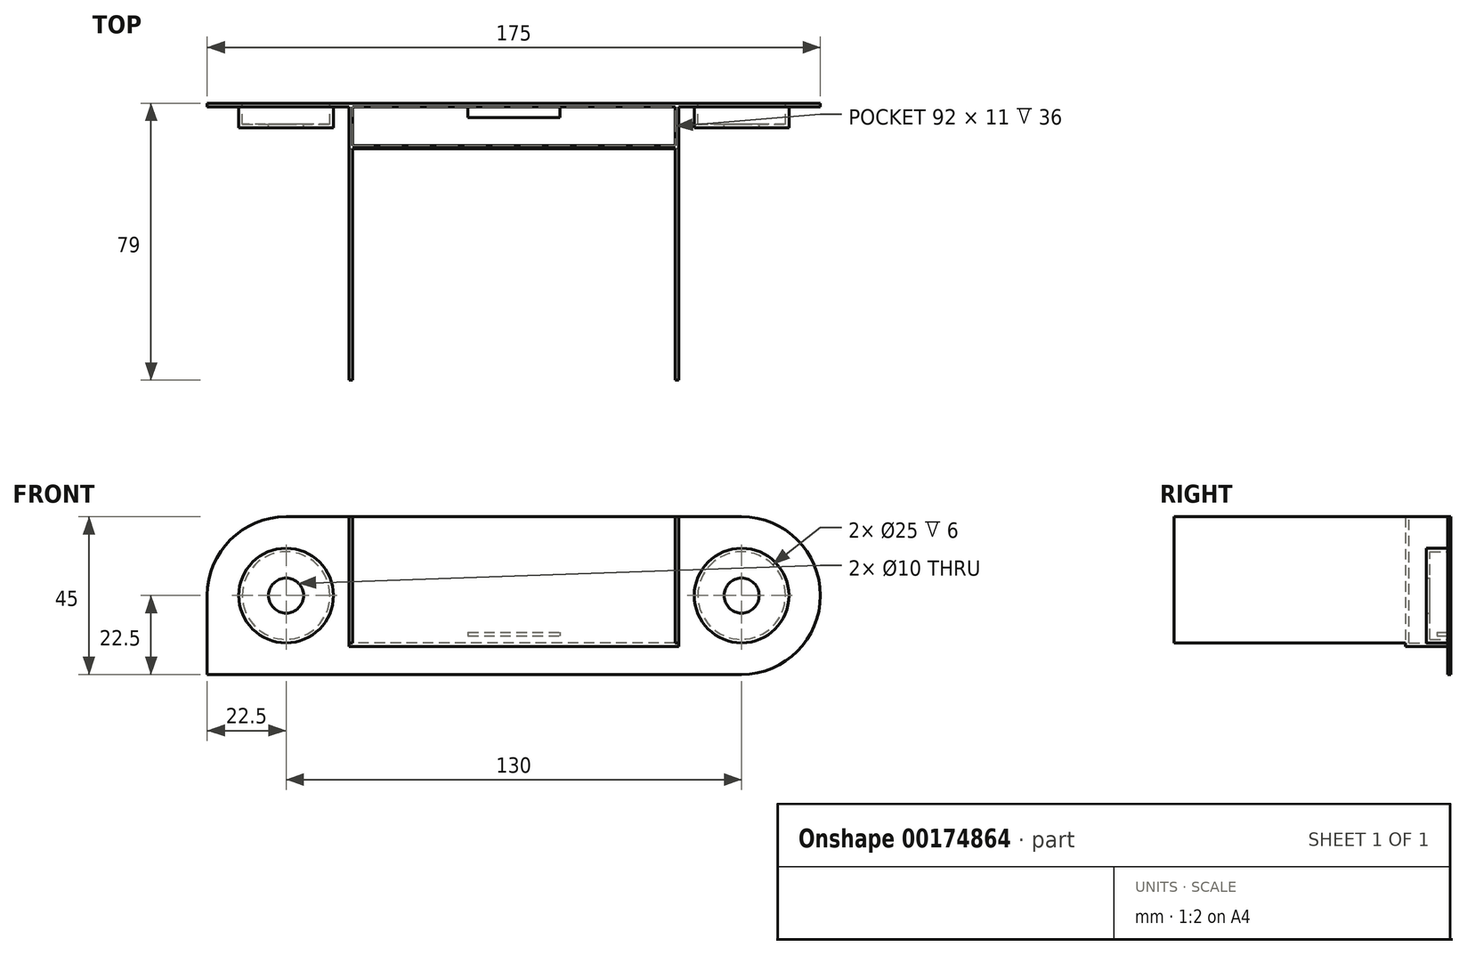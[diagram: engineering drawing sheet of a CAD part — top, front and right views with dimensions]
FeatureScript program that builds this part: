
annotation { "Feature Type Name" : "Feature", "Feature Type Description" : "" }
export const myFeature = defineFeature(function(context is Context, id is Id, definition is map)
    precondition{}
    {
        {
            var Q0;
            Q0=qCreatedBy(makeId("Front.planeOp"),FACE);
            var sketch = newSketch(context, id + "F0", { "sketchPlane" : qUnion([Q0])});
            skLineSegment(sketch, "E0.bottom", {"start": v(82.5, 22.5) * mm, "end": v(-82.5, 22.5) * mm});
            skLineSegment(sketch, "E0.top", {"start": v(82.5, -22.5) * mm, "end": v(-82.5, -22.5) * mm});
            skLineSegment(sketch, "E0.left", {"start": v(82.5, 22.5) * mm, "end": v(82.5, -22.5) * mm});
            skLineSegment(sketch, "E0.right", {"start": v(-82.5, 22.5) * mm, "end": v(-82.5, -22.5) * mm});
            skPoint(sketch, "E0.middle", {"position": v(0, 0) * mm});
            skCircle(sketch, "E1", {"center": v(-65, 0) * mm, "radius": 12.5 * mm});
            skCircle(sketch, "E2", {"center": v(65, 0) * mm, "radius": 12.5 * mm});
            skSolve(sketch);
        }
        {
            var Q0;
            Q0=qSketchRegion(id+"F0",true);
            extrude(context, id + "F1", {"entities" : qUnion([Q0]), "depth" : 1 * mm});
        }
        {
            var Q0;
            Q0=makeQuery(id+"F1.opExtrude","CAP_FACE",FACE,{"disambiguationData":[OSD([sQuery(id+"F0.wireOp",EDGE,"E0.bottom"),sQuery(id+"F0.wireOp",EDGE,"E0.top"),sQuery(id+"F0.wireOp",EDGE,"E0.left"),sQuery(id+"F0.wireOp",EDGE,"E0.right"),sQuery(id+"F0.wireOp",EDGE,"E1"),sQuery(id+"F0.wireOp",EDGE,"E2")])],"isStart":false});
            var sketch = newSketch(context, id + "F2", { "sketchPlane" : qUnion([Q0])});
            skArc(sketch, "E3", {"start": v(65, -22.5) * mm, "mid": v(87.5, 0) * mm, "end": v(65, 22.5) * mm});
            skPoint(sketch, "E4.end.orphan", {"position": v(-82.5, 0) * mm});
            skArc(sketch, "E5", {"start": v(-65, 22.5) * mm, "mid": v(-87.5, 0) * mm, "end": v(-65, -22.5) * mm});
            skLineSegment(sketch, "E6", {"start": v(-65, 22.5) * mm, "end": v(-65, 14.96) * mm});
            skLineSegment(sketch, "E7", {"start": v(-65, 14.96) * mm, "end": v(-75.45, 11.76) * mm});
            skLineSegment(sketch, "E8", {"start": v(-75.45, 11.76) * mm, "end": v(-79.56, 6.47) * mm});
            skLineSegment(sketch, "E9", {"start": v(-79.56, 6.47) * mm, "end": v(-79.56, 0) * mm});
            skLineSegment(sketch, "E10", {"start": v(-79.56, 0) * mm, "end": v(-76.59, -7.8) * mm});
            skLineSegment(sketch, "E11", {"start": v(-76.59, -7.8) * mm, "end": v(-72.84, -12.91) * mm});
            skLineSegment(sketch, "E12", {"start": v(-72.84, -12.91) * mm, "end": v(-67.48, -15.7) * mm});
            skLineSegment(sketch, "E13", {"start": v(-67.48, -15.7) * mm, "end": v(-65, -22.5) * mm});
            skLineSegment(sketch, "E14", {"start": v(65, 22.5) * mm, "end": v(71.47, 16.28) * mm});
            skLineSegment(sketch, "E15", {"start": v(71.47, 16.28) * mm, "end": v(77.4, 9.11) * mm});
            skLineSegment(sketch, "E16", {"start": v(77.4, 9.11) * mm, "end": v(80.4, 2.14) * mm});
            skLineSegment(sketch, "E17", {"start": v(80.4, 2.14) * mm, "end": v(80.4, -5.23) * mm});
            skLineSegment(sketch, "E18", {"start": v(80.4, -5.23) * mm, "end": v(78.4, -12.15) * mm});
            skLineSegment(sketch, "E19", {"start": v(78.4, -12.15) * mm, "end": v(74.66, -14.4) * mm});
            skLineSegment(sketch, "E20", {"start": v(74.66, -14.4) * mm, "end": v(68.4, -19.1) * mm});
            skLineSegment(sketch, "E21", {"start": v(68.4, -19.1) * mm, "end": v(65, -22.5) * mm});
            skSolve(sketch);
        }
        {
            var Q0;
            Q0=qSketchRegion(id+"F2",true);
            extrude(context, id + "F3", {"entities" : qUnion([Q0]), "operationType" : NewBodyOperationType.ADD, "oppositeDirection" : true, "depth" : 1 * mm});
        }
        {
            var Q0;
            {var subQ1=makeQuery(id+"F1.opExtrude","CAP_EDGE",EDGE,{"disambiguationData":[OSD([sQuery(id+"F0.wireOp",EDGE,"E0.bottom")])],"isStart":false});var subQ3=makeQuery(id+"F1.opExtrude","CAP_EDGE",EDGE,{"disambiguationData":[OSD([sQuery(id+"F0.wireOp",EDGE,"E0.right")])],"isStart":false});var subQ5=makeQuery(id+"F2.imprint","INTERSECT",VERTEX,{"derivedFrom":[subQ1,subQ3]});Q0=makeQuery(id+"F2.imprint","IMPRINT",FACE,{"disambiguationData":[TD([[makeQuery(id+"F2.imprint","IMPRINT",EDGE,{"disambiguationData":[TD([[subQ5,-1.0]])],"derivedFrom":subQ3}),1.0]])]});}
            extrude(context, id + "F4", {"entities" : qUnion([Q0]), "operationType" : NewBodyOperationType.REMOVE, "oppositeDirection" : true, "depth" : 25 * mm});
        }
        {
            var Q0;
            {var subQ1=makeQuery(id+"F1.opExtrude","CAP_EDGE",EDGE,{"disambiguationData":[OSD([sQuery(id+"F0.wireOp",EDGE,"E0.top")])],"isStart":false});var subQ3=makeQuery(id+"F1.opExtrude","CAP_EDGE",EDGE,{"disambiguationData":[OSD([sQuery(id+"F0.wireOp",EDGE,"E0.left")])],"isStart":false});var subQ5=makeQuery(id+"F2.imprint","INTERSECT",VERTEX,{"derivedFrom":[subQ1,subQ3]});Q0=makeQuery(id+"F2.imprint","IMPRINT",FACE,{"disambiguationData":[TD([[makeQuery(id+"F2.imprint","IMPRINT",EDGE,{"disambiguationData":[TD([[subQ5,1.0]])],"derivedFrom":subQ3}),-1.0]])]});}
            var Q1;
            {var subQ1=makeQuery(id+"F1.opExtrude","CAP_EDGE",EDGE,{"disambiguationData":[OSD([sQuery(id+"F0.wireOp",EDGE,"E0.bottom")])],"isStart":false});var subQ3=makeQuery(id+"F1.opExtrude","CAP_EDGE",EDGE,{"disambiguationData":[OSD([sQuery(id+"F0.wireOp",EDGE,"E0.left")])],"isStart":false});var subQ5=makeQuery(id+"F2.imprint","INTERSECT",VERTEX,{"derivedFrom":[subQ1,subQ3]});Q1=makeQuery(id+"F2.imprint","IMPRINT",FACE,{"disambiguationData":[TD([[makeQuery(id+"F2.imprint","IMPRINT",EDGE,{"disambiguationData":[TD([[subQ5,-1.0]])],"derivedFrom":subQ3}),-1.0]])]});}
            var Q2;
            {var subQ1=makeQuery(id+"F1.opExtrude","CAP_EDGE",EDGE,{"disambiguationData":[OSD([sQuery(id+"F0.wireOp",EDGE,"E0.top")])],"isStart":false});var subQ3=makeQuery(id+"F1.opExtrude","CAP_EDGE",EDGE,{"disambiguationData":[OSD([sQuery(id+"F0.wireOp",EDGE,"E0.right")])],"isStart":false});var subQ5=makeQuery(id+"F2.imprint","INTERSECT",VERTEX,{"derivedFrom":[subQ1,subQ3]});Q2=makeQuery(id+"F2.imprint","IMPRINT",FACE,{"disambiguationData":[TD([[makeQuery(id+"F2.imprint","IMPRINT",EDGE,{"disambiguationData":[TD([[subQ5,1.0]])],"derivedFrom":subQ3}),1.0]])]});}
            extrude(context, id + "F5", {"entities" : qUnion([Q0, Q1, Q2]), "operationType" : NewBodyOperationType.REMOVE, "oppositeDirection" : true, "depth" : 25 * mm});
        }
        {
            var Q0;
            Q0=makeQuery(id+"F3.boolean.opBoolean","MERGE",FACE,{"derivedFrom":[makeQuery(id+"F1.opExtrude","CAP_FACE",FACE,{"disambiguationData":[OSD([sQuery(id+"F0.wireOp",EDGE,"E0.bottom"),sQuery(id+"F0.wireOp",EDGE,"E0.top"),sQuery(id+"F0.wireOp",EDGE,"E0.left"),sQuery(id+"F0.wireOp",EDGE,"E0.right"),sQuery(id+"F0.wireOp",EDGE,"E1"),sQuery(id+"F0.wireOp",EDGE,"E2")])],"isStart":false}),makeQuery(id+"F3.opExtrude","CAP_FACE",FACE,{"disambiguationData":[OSD([sQuery(id+"F2.wireOp",EDGE,"E3"),sQuery(id+"F2.wireOp",EDGE,"E14"),sQuery(id+"F2.wireOp",EDGE,"E15"),sQuery(id+"F2.wireOp",EDGE,"E16"),sQuery(id+"F2.wireOp",EDGE,"E17"),sQuery(id+"F2.wireOp",EDGE,"E18"),sQuery(id+"F2.wireOp",EDGE,"E19"),sQuery(id+"F2.wireOp",EDGE,"E20"),sQuery(id+"F2.wireOp",EDGE,"E21")])],"isStart":true}),makeQuery(id+"F3.opExtrude","CAP_FACE",FACE,{"disambiguationData":[OSD([sQuery(id+"F2.wireOp",EDGE,"E5"),sQuery(id+"F2.wireOp",EDGE,"E6"),sQuery(id+"F2.wireOp",EDGE,"E7"),sQuery(id+"F2.wireOp",EDGE,"E8"),sQuery(id+"F2.wireOp",EDGE,"E9"),sQuery(id+"F2.wireOp",EDGE,"E10"),sQuery(id+"F2.wireOp",EDGE,"E11"),sQuery(id+"F2.wireOp",EDGE,"E12"),sQuery(id+"F2.wireOp",EDGE,"E13")])],"isStart":true})]});
            var sketch = newSketch(context, id + "F6", { "sketchPlane" : qUnion([Q0])});
            skCircle(sketch, "E22", {"center": v(-65, 0) * mm, "radius": 12.5 * mm});
            skCircle(sketch, "E23", {"center": v(-65, 0) * mm, "radius": 13.5 * mm});
            skCircle(sketch, "E24", {"center": v(65, 0) * mm, "radius": 12.5 * mm});
            skCircle(sketch, "E25", {"center": v(65, 0) * mm, "radius": 13.5 * mm});
            skSolve(sketch);
        }
        {
            var Q0;
            Q0=qSketchRegion(id+"F6",true);
            extrude(context, id + "F7", {"entities" : qUnion([Q0]), "operationType" : NewBodyOperationType.ADD, "depth" : 5 * mm});
        }
        {
            var Q0;
            Q0=makeQuery(id+"F7.opExtrude","CAP_FACE",FACE,{"disambiguationData":[OSD([sQuery(id+"F6.wireOp",EDGE,"E22"),sQuery(id+"F6.wireOp",EDGE,"E23")])],"isStart":false});
            var sketch = newSketch(context, id + "F8", { "sketchPlane" : qUnion([Q0])});
            skCircle(sketch, "E26", {"center": v(-65, 0) * mm, "radius": 13.5 * mm});
            skCircle(sketch, "E27", {"center": v(-65, 0) * mm, "radius": 5 * mm});
            skCircle(sketch, "E28", {"center": v(65, 0) * mm, "radius": 13.5 * mm});
            skCircle(sketch, "E29", {"center": v(65, 0) * mm, "radius": 5 * mm});
            skSolve(sketch);
        }
        {
            var Q0;
            Q0=qSketchRegion(id+"F8",true);
            extrude(context, id + "F9", {"entities" : qUnion([Q0]), "operationType" : NewBodyOperationType.ADD, "depth" : 1 * mm});
        }
        {
            var Q0;
            Q0=makeQuery(id+"F3.boolean.opBoolean","MERGE",FACE,{"derivedFrom":[makeQuery(id+"F1.opExtrude","CAP_FACE",FACE,{"disambiguationData":[OSD([sQuery(id+"F0.wireOp",EDGE,"E0.bottom"),sQuery(id+"F0.wireOp",EDGE,"E0.top"),sQuery(id+"F0.wireOp",EDGE,"E0.left"),sQuery(id+"F0.wireOp",EDGE,"E0.right"),sQuery(id+"F0.wireOp",EDGE,"E1"),sQuery(id+"F0.wireOp",EDGE,"E2")])],"isStart":false}),makeQuery(id+"F3.opExtrude","CAP_FACE",FACE,{"disambiguationData":[OSD([sQuery(id+"F2.wireOp",EDGE,"E3"),sQuery(id+"F2.wireOp",EDGE,"E14"),sQuery(id+"F2.wireOp",EDGE,"E15"),sQuery(id+"F2.wireOp",EDGE,"E16"),sQuery(id+"F2.wireOp",EDGE,"E17"),sQuery(id+"F2.wireOp",EDGE,"E18"),sQuery(id+"F2.wireOp",EDGE,"E19"),sQuery(id+"F2.wireOp",EDGE,"E20"),sQuery(id+"F2.wireOp",EDGE,"E21")])],"isStart":true}),makeQuery(id+"F3.opExtrude","CAP_FACE",FACE,{"disambiguationData":[OSD([sQuery(id+"F2.wireOp",EDGE,"E5"),sQuery(id+"F2.wireOp",EDGE,"E6"),sQuery(id+"F2.wireOp",EDGE,"E7"),sQuery(id+"F2.wireOp",EDGE,"E8"),sQuery(id+"F2.wireOp",EDGE,"E9"),sQuery(id+"F2.wireOp",EDGE,"E10"),sQuery(id+"F2.wireOp",EDGE,"E11"),sQuery(id+"F2.wireOp",EDGE,"E12"),sQuery(id+"F2.wireOp",EDGE,"E13")])],"isStart":true})]});
            var sketch = newSketch(context, id + "F10", { "sketchPlane" : qUnion([Q0])});
            skLineSegment(sketch, "E30.bottom", {"start": v(-87.5, 0) * mm, "end": v(-81.94, 0) * mm});
            skLineSegment(sketch, "E30.top", {"start": v(-87.5, -22.5) * mm, "end": v(-65, -22.5) * mm});
            skLineSegment(sketch, "E30.left", {"start": v(-87.5, 0) * mm, "end": v(-87.5, -22.5) * mm});
            skLineSegment(sketch, "E30.right", {"start": v(-65, -18.59) * mm, "end": v(-65, -22.5) * mm});
            skLineSegment(sketch, "E31", {"start": v(-81.94, 0) * mm, "end": v(-80.2, -9.62) * mm});
            skLineSegment(sketch, "E32", {"start": v(-80.2, -9.62) * mm, "end": v(-73.32, -16) * mm});
            skLineSegment(sketch, "E33", {"start": v(-73.32, -16) * mm, "end": v(-65, -18.59) * mm});
            skSolve(sketch);
        }
        {
            var Q0;
            Q0=qSketchRegion(id+"F10",true);
            extrude(context, id + "F11", {"entities" : qUnion([Q0]), "operationType" : NewBodyOperationType.ADD, "oppositeDirection" : true, "depth" : 1 * mm});
        }
        {
            var Q0;
            Q0=makeQuery(id+"F11.boolean.opBoolean","MERGE",FACE,{"derivedFrom":[makeQuery(id+"F3.boolean.opBoolean","MERGE",FACE,{"derivedFrom":[makeQuery(id+"F1.opExtrude","CAP_FACE",FACE,{"disambiguationData":[OSD([sQuery(id+"F0.wireOp",EDGE,"E0.bottom"),sQuery(id+"F0.wireOp",EDGE,"E0.top"),sQuery(id+"F0.wireOp",EDGE,"E0.left"),sQuery(id+"F0.wireOp",EDGE,"E0.right"),sQuery(id+"F0.wireOp",EDGE,"E1"),sQuery(id+"F0.wireOp",EDGE,"E2")])],"isStart":false}),makeQuery(id+"F3.opExtrude","CAP_FACE",FACE,{"disambiguationData":[OSD([sQuery(id+"F2.wireOp",EDGE,"E3"),sQuery(id+"F2.wireOp",EDGE,"E14"),sQuery(id+"F2.wireOp",EDGE,"E15"),sQuery(id+"F2.wireOp",EDGE,"E16"),sQuery(id+"F2.wireOp",EDGE,"E17"),sQuery(id+"F2.wireOp",EDGE,"E18"),sQuery(id+"F2.wireOp",EDGE,"E19"),sQuery(id+"F2.wireOp",EDGE,"E20"),sQuery(id+"F2.wireOp",EDGE,"E21")])],"isStart":true}),makeQuery(id+"F3.opExtrude","CAP_FACE",FACE,{"disambiguationData":[OSD([sQuery(id+"F2.wireOp",EDGE,"E5"),sQuery(id+"F2.wireOp",EDGE,"E6"),sQuery(id+"F2.wireOp",EDGE,"E7"),sQuery(id+"F2.wireOp",EDGE,"E8"),sQuery(id+"F2.wireOp",EDGE,"E9"),sQuery(id+"F2.wireOp",EDGE,"E10"),sQuery(id+"F2.wireOp",EDGE,"E11"),sQuery(id+"F2.wireOp",EDGE,"E12"),sQuery(id+"F2.wireOp",EDGE,"E13")])],"isStart":true})]}),makeQuery(id+"F11.opExtrude","CAP_FACE",FACE,{"disambiguationData":[OSD([sQuery(id+"F10.wireOp",EDGE,"E30.bottom"),sQuery(id+"F10.wireOp",EDGE,"E30.top"),sQuery(id+"F10.wireOp",EDGE,"E30.left"),sQuery(id+"F10.wireOp",EDGE,"E30.right"),sQuery(id+"F10.wireOp",EDGE,"E31"),sQuery(id+"F10.wireOp",EDGE,"E32"),sQuery(id+"F10.wireOp",EDGE,"E33")])],"isStart":true})]});
            var sketch = newSketch(context, id + "F12", { "sketchPlane" : qUnion([Q0])});
            skLineSegment(sketch, "E34.bottom", {"start": v(47, -13.5) * mm, "end": v(-47, -13.5) * mm});
            skLineSegment(sketch, "E34.top", {"start": v(47, -14.5) * mm, "end": v(-47, -14.5) * mm});
            skLineSegment(sketch, "E34.left", {"start": v(47, -13.5) * mm, "end": v(47, -14.5) * mm});
            skLineSegment(sketch, "E34.right", {"start": v(-47, -13.5) * mm, "end": v(-47, -14.5) * mm});
            skPoint(sketch, "E34.middle", {"position": v(0, -14) * mm});
            skLineSegment(sketch, "E35.bottom", {"start": v(-47, -14.5) * mm, "end": v(-46, -14.5) * mm});
            skLineSegment(sketch, "E35.top", {"start": v(-47, 22.5) * mm, "end": v(-46, 22.5) * mm});
            skLineSegment(sketch, "E35.left", {"start": v(-47, -14.5) * mm, "end": v(-47, 22.5) * mm});
            skLineSegment(sketch, "E35.right", {"start": v(-46, -14.5) * mm, "end": v(-46, 22.5) * mm});
            skLineSegment(sketch, "E36.bottom", {"start": v(47, -14.5) * mm, "end": v(46, -14.5) * mm});
            skLineSegment(sketch, "E36.top", {"start": v(47, 22.5) * mm, "end": v(46, 22.5) * mm});
            skLineSegment(sketch, "E36.left", {"start": v(47, -14.5) * mm, "end": v(47, 22.5) * mm});
            skLineSegment(sketch, "E36.right", {"start": v(46, -14.5) * mm, "end": v(46, 22.5) * mm});
            skSolve(sketch);
        }
        {
            var Q0;
            Q0 = qSketchRegion(id + "F12", true);
            extrude(context, id + "F13", {"entities" : qUnion([Q0]), "operationType" : NewBodyOperationType.ADD, "depth" : 11 * mm});
        }
        {
            var Q0;
            Q0=makeQuery(id+"F13.opExtrude","CAP_FACE",FACE,{"disambiguationData":[OSD([sQuery(id+"F12.wireOp",EDGE,"E34.bottom"),sQuery(id+"F12.wireOp",EDGE,"E34.top"),sQuery(id+"F12.wireOp",EDGE,"E35.bottom"),sQuery(id+"F12.wireOp",EDGE,"E35.top"),sQuery(id+"F12.wireOp",EDGE,"E35.left"),sQuery(id+"F12.wireOp",EDGE,"E35.right"),sQuery(id+"F12.wireOp",EDGE,"E36.bottom"),sQuery(id+"F12.wireOp",EDGE,"E36.top"),sQuery(id+"F12.wireOp",EDGE,"E36.left"),sQuery(id+"F12.wireOp",EDGE,"E36.right")])],"isStart":false});
            var sketch = newSketch(context, id + "F14", { "sketchPlane" : qUnion([Q0])});
            skLineSegment(sketch, "E37.bottom", {"start": v(-47, -14.5) * mm, "end": v(47, -14.5) * mm});
            skLineSegment(sketch, "E37.top", {"start": v(-47, 22.5) * mm, "end": v(47, 22.5) * mm});
            skLineSegment(sketch, "E37.left", {"start": v(-47, -14.5) * mm, "end": v(-47, 22.5) * mm});
            skLineSegment(sketch, "E37.right", {"start": v(47, -14.5) * mm, "end": v(47, 22.5) * mm});
            skSolve(sketch);
        }
        {
            var Q0;
            Q0 = qSketchRegion(id + "F14", true);
            extrude(context, id + "F15", {"entities" : qUnion([Q0]), "operationType" : NewBodyOperationType.ADD, "depth" : 1 * mm});
        }
        {
            var Q0;
            Q0=makeQuery(id+"F15.opExtrude","CAP_FACE",FACE,{"disambiguationData":[OSD([sQuery(id+"F14.wireOp",EDGE,"E37.bottom"),sQuery(id+"F14.wireOp",EDGE,"E37.top"),sQuery(id+"F14.wireOp",EDGE,"E37.left"),sQuery(id+"F14.wireOp",EDGE,"E37.right")])],"isStart":false});
            var sketch = newSketch(context, id + "F16", { "sketchPlane" : qUnion([Q0])});
            skLineSegment(sketch, "E38.bottom", {"start": v(-47, 22.5) * mm, "end": v(-46, 22.5) * mm});
            skLineSegment(sketch, "E38.top", {"start": v(-47, -13.5) * mm, "end": v(-46, -13.5) * mm});
            skLineSegment(sketch, "E38.left", {"start": v(-47, 22.5) * mm, "end": v(-47, -13.5) * mm});
            skLineSegment(sketch, "E38.right", {"start": v(-46, 22.5) * mm, "end": v(-46, -13.5) * mm});
            skLineSegment(sketch, "E39.bottom", {"start": v(47, 22.5) * mm, "end": v(46, 22.5) * mm});
            skLineSegment(sketch, "E39.top", {"start": v(47, -13.5) * mm, "end": v(46, -13.5) * mm});
            skLineSegment(sketch, "E39.left", {"start": v(47, 22.5) * mm, "end": v(47, -13.5) * mm});
            skLineSegment(sketch, "E39.right", {"start": v(46, 22.5) * mm, "end": v(46, -13.5) * mm});
            skSolve(sketch);
        }
        {
            var Q0;
            Q0 = qSketchRegion(id + "F16", true);
            extrude(context, id + "F17", {"entities" : qUnion([Q0]), "operationType" : NewBodyOperationType.ADD, "depth" : 66 * mm});
        }
        {
            var Q0;
            {var subQ0=sQuery(id+"F2.wireOp",EDGE,"E14");var subQ1=sQuery(id+"F2.wireOp",EDGE,"E3");var subQ2=sQuery(id+"F0.wireOp",EDGE,"E0.bottom");var subQ3=sQuery(id+"F0.wireOp",EDGE,"E0.left");var subQ5=sQuery(id+"F2.wireOp",EDGE,"E21");var subQ6=sQuery(id+"F0.wireOp",EDGE,"E0.top");var subQ7=sQuery(id+"F2.wireOp",EDGE,"E5");var subQ8=sQuery(id+"F10.wireOp",EDGE,"E30.top");var subQ9=sQuery(id+"F10.wireOp",EDGE,"E30.left");Q0=makeQuery(id+"F13.boolean.opBoolean","SPLIT",FACE,{"disambiguationData":[TD([makeQuery(id+"F1.opExtrude","SWEPT_FACE",FACE,{"disambiguationData":[OSD([subQ6])]})])],"derivedFrom":makeQuery(id+"F11.boolean.opBoolean","MERGE",FACE,{"derivedFrom":[makeQuery(id+"F3.boolean.opBoolean","MERGE",FACE,{"derivedFrom":[makeQuery(id+"F1.opExtrude","CAP_FACE",FACE,{"disambiguationData":[OSD([subQ2,subQ6,subQ3,sQuery(id+"F0.wireOp",EDGE,"E0.right"),sQuery(id+"F0.wireOp",EDGE,"E1"),sQuery(id+"F0.wireOp",EDGE,"E2")])],"isStart":false}),makeQuery(id+"F3.opExtrude","CAP_FACE",FACE,{"disambiguationData":[OSD([subQ1,subQ0,sQuery(id+"F2.wireOp",EDGE,"E15"),sQuery(id+"F2.wireOp",EDGE,"E16"),sQuery(id+"F2.wireOp",EDGE,"E17"),sQuery(id+"F2.wireOp",EDGE,"E18"),sQuery(id+"F2.wireOp",EDGE,"E19"),sQuery(id+"F2.wireOp",EDGE,"E20"),subQ5])],"isStart":true}),makeQuery(id+"F3.opExtrude","CAP_FACE",FACE,{"disambiguationData":[OSD([subQ7,sQuery(id+"F2.wireOp",EDGE,"E6"),sQuery(id+"F2.wireOp",EDGE,"E7"),sQuery(id+"F2.wireOp",EDGE,"E8"),sQuery(id+"F2.wireOp",EDGE,"E9"),sQuery(id+"F2.wireOp",EDGE,"E10"),sQuery(id+"F2.wireOp",EDGE,"E11"),sQuery(id+"F2.wireOp",EDGE,"E12"),sQuery(id+"F2.wireOp",EDGE,"E13")])],"isStart":true})]}),makeQuery(id+"F11.opExtrude","CAP_FACE",FACE,{"disambiguationData":[OSD([sQuery(id+"F10.wireOp",EDGE,"E30.bottom"),subQ8,subQ9,sQuery(id+"F10.wireOp",EDGE,"E30.right"),sQuery(id+"F10.wireOp",EDGE,"E31"),sQuery(id+"F10.wireOp",EDGE,"E32"),sQuery(id+"F10.wireOp",EDGE,"E33")])],"isStart":true})]})});}
            var sketch = newSketch(context, id + "F18", { "sketchPlane" : qUnion([Q0])});
            skLineSegment(sketch, "E40.bottom", {"start": v(-13.08, -10.5) * mm, "end": v(13.2, -10.5) * mm});
            skLineSegment(sketch, "E40.top", {"start": v(-13.08, -11.5) * mm, "end": v(13.2, -11.5) * mm});
            skLineSegment(sketch, "E40.left", {"start": v(-13.08, -10.5) * mm, "end": v(-13.08, -11.5) * mm});
            skLineSegment(sketch, "E40.right", {"start": v(13.2, -10.5) * mm, "end": v(13.2, -11.5) * mm});
            skSolve(sketch);
        }
        {
            var Q0;
            Q0 = qSketchRegion(id + "F18", true);
            extrude(context, id + "F19", {"entities" : qUnion([Q0]), "operationType" : NewBodyOperationType.ADD, "depth" : 3 * mm});
        }
    });
